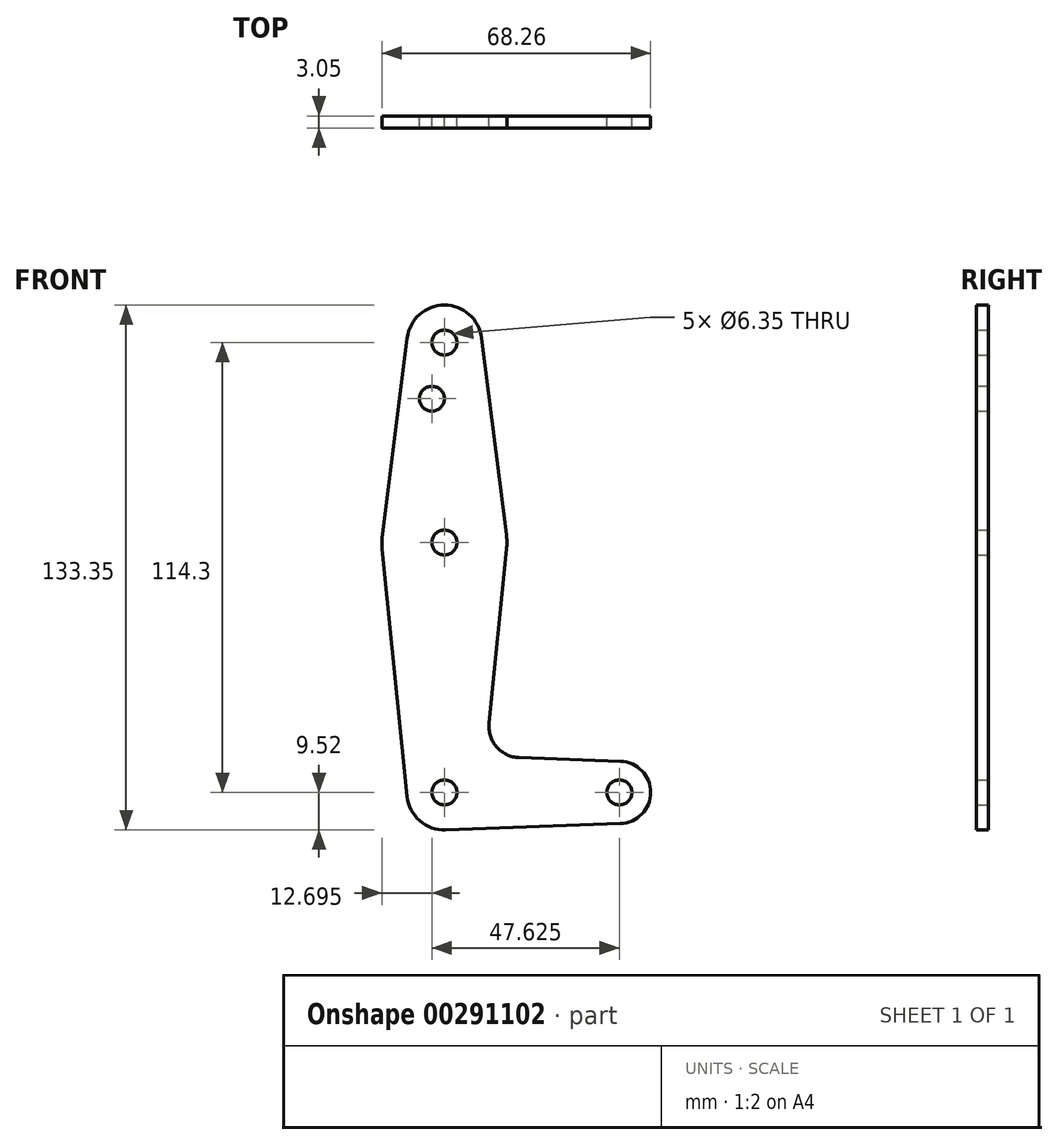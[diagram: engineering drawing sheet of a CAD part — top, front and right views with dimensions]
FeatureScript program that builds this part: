
annotation { "Feature Type Name" : "Feature", "Feature Type Description" : "" }
export const myFeature = defineFeature(function(context is Context, id is Id, definition is map)
    precondition{}
    {
        {
            var Q0;
            Q0=qCreatedBy(makeId("Front.planeOp"),FACE);
            var sketch = newSketch(context, id + "F0", { "sketchPlane" : qUnion([Q0])});
            skCircle(sketch, "E0", {"center": v(0, 0) * mm, "radius": 9.53 * mm});
            skLineSegment(sketch, "E1", {"start": v(0, 0) * mm, "end": v(44.45, 0) * mm, "construction": true});
            skLineSegment(sketch, "E2", {"start": v(0, 0) * mm, "end": v(0, 114.3) * mm, "construction": true});
            skCircle(sketch, "E3", {"center": v(0, 114.3) * mm, "radius": 9.53 * mm});
            skCircle(sketch, "E4", {"center": v(0, 63.5) * mm, "radius": 15.88 * mm});
            skCircle(sketch, "E5", {"center": v(44.45, 0) * mm, "radius": 7.94 * mm});
            skLineSegment(sketch, "E6", {"start": v(18.97, 8.85) * mm, "end": v(44.73, 7.93) * mm});
            skLineSegment(sketch, "E7", {"start": v(0.34, -9.52) * mm, "end": v(44.73, -7.93) * mm});
            skLineSegment(sketch, "E8", {"start": v(9.45, 115.5) * mm, "end": v(15.75, 65.48) * mm});
            skLineSegment(sketch, "E9", {"start": v(-9.45, 115.5) * mm, "end": v(-15.75, 65.48) * mm});
            skLineSegment(sketch, "E10", {"start": v(-15.8, 61.91) * mm, "end": v(-9.48, -0.95) * mm});
            skLineSegment(sketch, "E11", {"start": v(15.8, 61.91) * mm, "end": v(11.34, 17.6) * mm});
            skCircle(sketch, "E12", {"center": v(0, 114.3) * mm, "radius": 3.18 * mm});
            skCircle(sketch, "E13", {"center": v(0, 63.5) * mm, "radius": 3.18 * mm});
            skCircle(sketch, "E14", {"center": v(0, 0) * mm, "radius": 3.18 * mm});
            skCircle(sketch, "E15", {"center": v(44.45, 0) * mm, "radius": 3.18 * mm});
            skCircle(sketch, "E16", {"center": v(-3.18, 100.03) * mm, "radius": 3.18 * mm});
            skArc(sketch, "E17.filletArc", {"start": v(11.34, 17.6) * mm, "mid": v(13.26, 11.57) * mm, "end": v(18.97, 8.85) * mm});
            skSolve(sketch);
        }
        {
            var Q0;
            Q0 = qSketchRegion(id + "F0", true);
            extrude(context, id + "F1", {"entities" : qUnion([Q0]), "depth" : 3.05 * mm});
        }
    });
